# Revit family: dd4743ba-0f4b-45d5-8a1c-17b8dde6486b
name_source: partatom
category: Plumbing Fixtures
units: mm (PartAtom-declared; Revit-internal decimal feet)

## family parameters
Cut with Voids When Loaded = No
Host = Face
OmniClass Number = 23.31.19.00
Part Type = Normal
Room Calculation Point = No
Round Connector Dimension = Use Diameter
Shared = No

## types (1)
- Not A Type-See Type Catalog
    ADA Compliant = Yes
    Assembly Code = D2010100
    CW Connection = Yes
    Cold Water Inlet = Cold Water Inlet
    Date Modified = 02/13/2019
    Default Elevation = 0"
    Finish = Default
    Flow Rate = 0 GPM
    Flush Rate = 1.6 GPF
    HW Connection = No
    Height = 32 1/2"
    Hot Water Inlet = Hot Water Inlet
    Left hand trip lever = No
    Length = 28 1/8"
    Manufacturer = KOHLER Co.
    MasterFormat 1995 = 15410
    MasterFormat 2004 = 22.41.13
    Material = Vitreous China
    Pressure = 0.00 psi
    Product Documentation Link = https://www.us.kohler.com
    Product Name = Persuade Curv
    Product Page URL = http://www.us.kohler.com
    Right hand trip lever = No
    Rough-In = 12"
    Seat Included = No
    Type = 0
    URL = https://www.us.kohler.com
    Vent Connection = No
    Waste Connection = Yes
    Waste Water Outlet = Waste Water Outlet
    WaterSense Certified = Yes
    Width = 14 3/16"

## geometry (parser evidence)
native form markers: Sweep x4
no freeform markers — native parametric forms only
